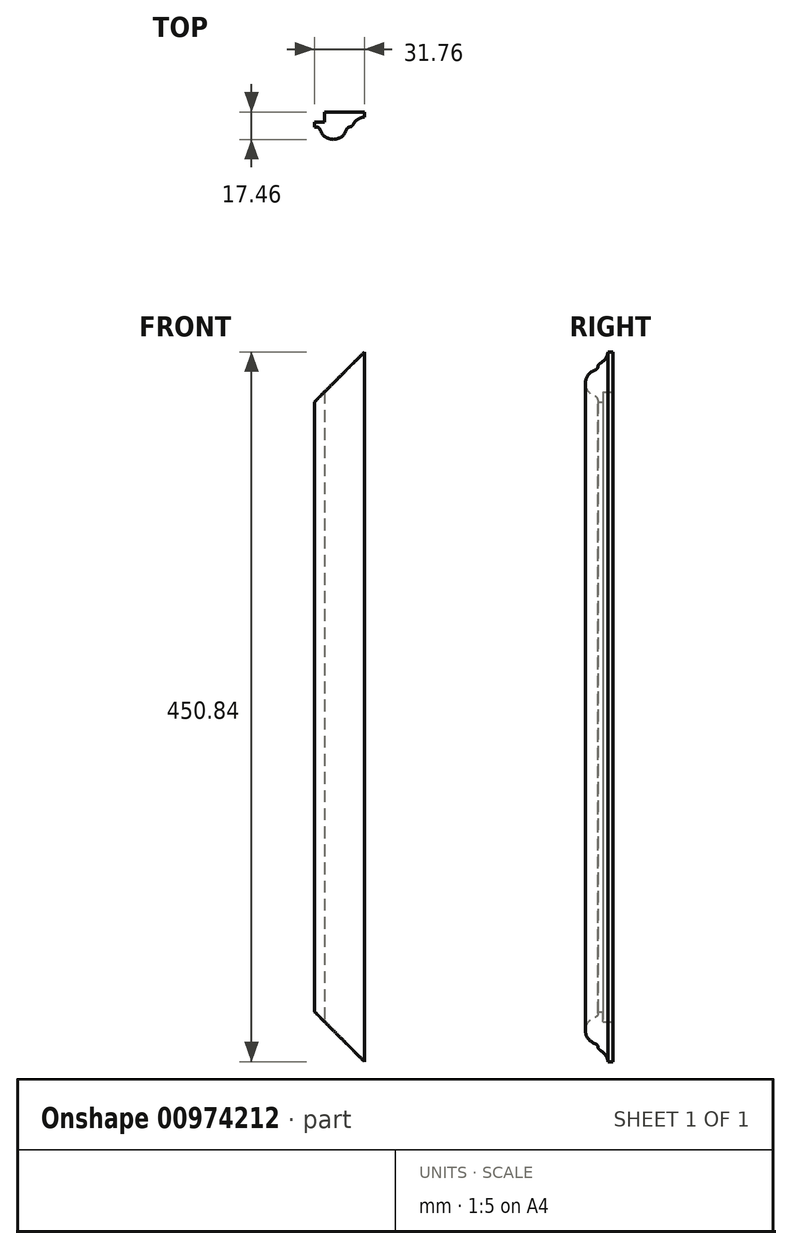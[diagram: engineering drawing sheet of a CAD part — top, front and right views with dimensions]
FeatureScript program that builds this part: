
annotation { "Feature Type Name" : "Feature", "Feature Type Description" : "" }
export const myFeature = defineFeature(function(context is Context, id is Id, definition is map)
    precondition{}
    {
        {
            var Q0;
            Q0=qCreatedBy(makeId("Top.planeOp"),FACE);
            var sketch = newSketch(context, id + "F0", { "sketchPlane" : qUnion([Q0])});
            skLineSegment(sketch, "E0.bottom", {"start": v(15.88, 8.73) * mm, "end": v(-15.88, 8.73) * mm});
            skLineSegment(sketch, "E0.top", {"start": v(-3.97, -8.73) * mm, "end": v(-3.98, -8.73) * mm});
            skLineSegment(sketch, "E0.left", {"start": v(15.88, 8.73) * mm, "end": v(15.88, -0.8) * mm});
            skLineSegment(sketch, "E0.right", {"start": v(-15.88, 8.73) * mm, "end": v(-15.88, -0.8) * mm});
            skPoint(sketch, "E0.middle", {"position": v(0, 0) * mm});
            skLineSegment(sketch, "E1", {"start": v(15.88, 8.73) * mm, "end": v(15.88, 5.56) * mm});
            skLineSegment(sketch, "E2", {"start": v(-19.4, -0.8) * mm, "end": v(24.15, -0.8) * mm, "construction": true});
            skLineSegment(sketch, "E3", {"start": v(21.72, 5.56) * mm, "end": v(-20.21, 5.56) * mm, "construction": true});
            skPoint(sketch, "E4", {"position": v(7.94, -0.8) * mm});
            skPoint(sketch, "E5", {"position": v(4.76, -0.8) * mm});
            skPoint(sketch, "E6", {"position": v(-12.7, -0.8) * mm});
            skLineSegment(sketch, "E7", {"start": v(-15.88, -0.8) * mm, "end": v(-12.7, -0.8) * mm});
            skLineSegment(sketch, "E8", {"start": v(4.76, -0.8) * mm, "end": v(7.94, -0.8) * mm});
            skPoint(sketch, "E9", {"position": v(-3.98, -8.73) * mm});
            skArc(sketch, "E10", {"start": v(15.88, 5.56) * mm, "mid": v(10.99, 3.53) * mm, "end": v(7.94, -0.8) * mm});
            skArc(sketch, "E11", {"start": v(-12.7, -0.8) * mm, "mid": v(-3.97, -8.73) * mm, "end": v(4.76, -0.8) * mm});
            skPoint(sketch, "E12.orphan", {"position": v(-15.88, -8.73) * mm});
            skPoint(sketch, "E13.orphan", {"position": v(15.88, -8.73) * mm});
            skSolve(sketch);
        }
        {
            var Q0;
            Q0=makeQuery(id+"F0.imprint","IMPRINT",FACE,{"disambiguationData":[TD([[makeQuery(id+"F0.imprint","IMPRINT",EDGE,{"derivedFrom":sQuery(id+"F0.wireOp",EDGE,"E0.bottom")}),1.0]])]});
            extrude(context, id + "F1", {"entities" : qUnion([Q0]), "endBound" : BoundingType.SYMMETRIC, "depth" : 450.85 * mm, "offsetDistance" : 25.4 * mm});
        }
        {
            var Q0;
            Q0=makeQuery(id+"F1.opExtrude","SWEPT_EDGE",EDGE,{"disambiguationData":[OSD([sQuery(id+"F0.wireOp",EDGE,"E8"),sQuery(id+"F0.wireOp",EDGE,"E10")])]});
            fillet(context, id + "F2", {"entities" : qUnion([Q0]), "radius" : 2.54 * mm, "tangentPropagation" : true, "allowEdgeOverflow" : false});
        }
        {
            var Q0;
            Q0=makeQuery(id+"F1.opExtrude","SWEPT_EDGE",EDGE,{"disambiguationData":[OSD([sQuery(id+"F0.wireOp",EDGE,"E7"),sQuery(id+"F0.wireOp",EDGE,"E11")])]});
            fillet(context, id + "F3", {"entities" : qUnion([Q0]), "radius" : 2.54 * mm, "tangentPropagation" : true, "allowEdgeOverflow" : false});
        }
        {
            var Q0;
            Q0=makeQuery(id+"F1.opExtrude","SWEPT_EDGE",EDGE,{"disambiguationData":[OSD([sQuery(id+"F0.wireOp",EDGE,"E8"),sQuery(id+"F0.wireOp",EDGE,"E11")])]});
            fillet(context, id + "F4", {"entities" : qUnion([Q0]), "radius" : 2.54 * mm, "tangentPropagation" : true, "allowEdgeOverflow" : false});
        }
        {
            var Q0;
            Q0=makeQuery(id+"F1.opExtrude","SWEPT_FACE",FACE,{"disambiguationData":[OSD([sQuery(id+"F0.wireOp",EDGE,"E0.bottom")])]});
            var sketch = newSketch(context, id + "F5", { "sketchPlane" : qUnion([Q0])});
            skLineSegment(sketch, "E14.top", {"start": v(-15.88, 225.43) * mm, "end": v(15.88, 225.43) * mm});
            skLineSegment(sketch, "E15", {"start": v(-15.88, 225.43) * mm, "end": v(15.88, 193.68) * mm});
            skLineSegment(sketch, "E16", {"start": v(15.88, 193.68) * mm, "end": v(15.88, 225.43) * mm});
            skLineSegment(sketch, "E17.MirrorCS", {"start": v(-15.88, -225.43) * mm, "end": v(15.88, -225.43) * mm});
            skLineSegment(sketch, "E18.MirrorCS", {"start": v(-15.87, -225.43) * mm, "end": v(15.88, -193.68) * mm});
            skLineSegment(sketch, "E19.MirrorCS", {"start": v(15.88, -193.68) * mm, "end": v(15.88, -225.43) * mm});
            skSolve(sketch);
        }
        {
            var Q0;
            Q0=makeQuery(id+"F5.imprint","IMPRINT",FACE,{"disambiguationData":[TD([[makeQuery(id+"F5.imprint","IMPRINT",EDGE,{"derivedFrom":sQuery(id+"F5.wireOp",EDGE,"E14.top")}),-1.0]])]});
            var Q1;
            Q1=makeQuery(id+"F5.imprint","IMPRINT",FACE,{"disambiguationData":[TD([[makeQuery(id+"F5.imprint","IMPRINT",EDGE,{"derivedFrom":sQuery(id+"F5.wireOp",EDGE,"E17.MirrorCS")}),1.0]])]});
            extrude(context, id + "F6", {"entities" : qUnion([Q0, Q1]), "operationType" : NewBodyOperationType.REMOVE, "endBound" : BoundingType.THROUGH_ALL, "oppositeDirection" : true, "depth" : 25.4 * mm, "offsetDistance" : 25.4 * mm});
        }
        {
            var Q0;
            Q0=makeQuery(id+"F6.boolean.opBoolean","SPLIT",FACE,{"disambiguationData":[TD([makeQuery(id+"F6.opExtrude","SWEPT_FACE",FACE,{"disambiguationData":[OSD([sQuery(id+"F5.wireOp",EDGE,"E15")])]})])],"derivedFrom":makeQuery(id+"F1.opExtrude","SWEPT_FACE",FACE,{"disambiguationData":[OSD([sQuery(id+"F0.wireOp",EDGE,"E0.bottom")])]})});
            var sketch = newSketch(context, id + "F7", { "sketchPlane" : qUnion([Q0])});
            skLineSegment(sketch, "E20", {"start": v(9.52, 200.03) * mm, "end": v(9.52, -200.03) * mm});
            skLineSegment(sketch, "E21", {"start": v(9.52, -200.03) * mm, "end": v(15.88, -193.67) * mm});
            skLineSegment(sketch, "E22", {"start": v(15.88, -193.67) * mm, "end": v(15.87, 193.67) * mm});
            skLineSegment(sketch, "E23", {"start": v(15.88, 193.68) * mm, "end": v(9.52, 200.03) * mm});
            skSolve(sketch);
        }
        {
            var Q0;
            Q0=makeQuery(id+"F7.imprint","IMPRINT",FACE,{"disambiguationData":[TD([[makeQuery(id+"F7.imprint","IMPRINT",EDGE,{"derivedFrom":sQuery(id+"F7.wireOp",EDGE,"E20")}),1.0]])]});
            extrude(context, id + "F8", {"entities" : qUnion([Q0]), "operationType" : NewBodyOperationType.REMOVE, "oppositeDirection" : true, "depth" : 6.35 * mm, "offsetDistance" : 25.4 * mm});
        }
    });
